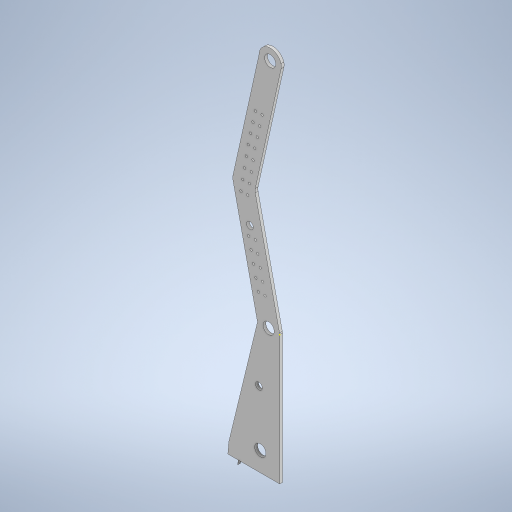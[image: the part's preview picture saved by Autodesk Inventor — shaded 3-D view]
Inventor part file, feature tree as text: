
AUTODESK INVENTOR PART (.ipt)
format: ipt  version: 2023 (Build 270158000, 158)  size: 542,720 bytes
history: native  units: in
note: dims shown in document units (in); Inventor stores cm internally (conversion verified against a paired STEP export)
features: sketch x17, extrude x15, fillet x1, projected_geometry x1
ambient origin geometry x8: Origin, YZ Plane, XZ Plane, XY Plane, X Axis, Y Axis, Z Axis, Center Point
bodies: Body1 (feature_tree), Body2 (feature_tree), Body3 (feature_tree)
feature tree (34):
  extrude  "Extrusion3"  Depth=0.7043in
  sketch  "Sketch3"  dims[d0=4.5in d1=0.7043in]
  extrude  "Extrusion14"  Depth=1.0651in
  extrude  "Extrusion15"  Depth=1.0in
  extrude  "Extrusion16"  Depth=0.5in
  extrude  "Extrusion17"  Depth=0.5in
  extrude  "Extrusion18"  Depth=0.5in
  extrude  "Extrusion19"  Depth=1.0in
  extrude  "Extrusion20"  Depth=0.5in
  sketch  "Sketch11"  dims[d25=0.5325in d26=1.0in]
  sketch  "Sketch12"  dims[d27=1.0in d28=0.5in d29=0.5in]
  fillet  "Fillet1"  Radius=0.5in
  sketch  "Sketch13"  dims[d30=0.25in d31=0.0in d42=1.0in]
  sketch  "Sketch33"  dims[d50=1.5in d51=0.25in]
  extrude  "Extrusion43"  Depth=1.0in
  extrude  "Extrusion44"  Depth=0.25in
  extrude  "Extrusion45"  Depth=0.585in
  extrude  "Extrusion46"  Depth=1.0in TaperAngle=0.0deg
  sketch  "Sketch41"  dims[d91=0.5in d92=0.5in]
  extrude  "Extrusion48"  Depth=1.0in TaperAngle=0.0deg
  extrude  "Extrusion49"  Depth=1.0in
  extrude  "Extrusion50"  Depth=0.5in
  sketch  "Sketch6"  dims[d2=4.5in d3=1.0651in]
  sketch  "Sketch7"  dims[d4=1.0in d5=1.0in]
  sketch  "Sketch8"  dims[d6=1.0in d7=0.5in]
  projected_geometry  "Projected Loop1"
  sketch  "Sketch9"  dims[d8=0.5in d9=0.5in]
  sketch  "Sketch10"  dims[d10=0.5in d24=5.5in]
  sketch  "Sketch37"  dims[d59=0.3in d76=0.585in]
  sketch  "Sketch38"  dims[d77=0.585in d78=1.0in d79=0.0in]
  sketch  "Sketch39"  dims[d82=0.1in d83=1.0in d84=0.0in]
  sketch  "Sketch40"  dims[d89=1.0in d90=0.5325in]
  sketch  "Sketch42"  dims[d93=0.5in]
  sketch  "Sketch43"  dims[d94=0.5in d95=0.1in d96=0.1in d97=0.1in d98=0.1in d99=0.1in d100=1.0in d101=0.0in d102=0.6in d103=0.1in d104=1.0in d105=0.0in d106=0.125in d107=0.0in d108=2.0in d109=0.3in d110=0.3in d111=0.3in d112=0.3in d113=0.3in d114=0.3in d115=0.3in d116=0.1in d117=0.1in d118=0.1in d119=0.1in d120=0.1in d121=0.1in d122=0.1in d123=0.5in d124=0.5in d125=0.5in d126=0.5in d127=0.5325in d128=0.5in d129=0.5in d130=0.3in d131=0.3in d132=0.3in d133=0.3in d134=0.3in d135=0.3in d136=0.3in d137=0.1in d138=0.1in d139=0.1in d140=0.1in d141=0.1in d142=0.1in d143=0.1in d144=0.1in d145=0.1in d146=0.1in d147=0.1in d148=0.1in d149=0.1in d150=0.1in d151=0.125in d152=0.0in d153=0.125in d154=0.0in d155=0.4in d240=6.0in d241=1.0in d242=0.125in d243=0.0in d244=0.125in d245=0.0in d246=0.2in d247=0.5in d248=0.125in d249=0.0in d250=0.5in d251=0.125in d252=0.0in d253=0.5in d257=0.5in d258=0.125in d259=0.0in d260=2.5in d261=0.6871in d262=0.3in d263=0.125in d264=0.0in d265=0.3in d266=0.1718in d267=0.585in d268=0.5in d269=0.5in d270=0.5in d271=0.125in d272=0.0in d60=0.0344in d61=0.5in d62=0.0344in d74=0.5in d75=0.0344in d80=0.5in d81=0.0344in d158=0.5in d159=0.0344in d160=0.5in d161=0.0344in d162=0.5in d163=0.0344in d164=0.5in d165=0.0344in d202=0.5in d203=0.0344in d204=0.5in d205=0.0344in d229=0.5in d230=0.0344in d231=0.5in d232=0.0344in]
